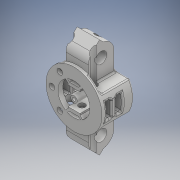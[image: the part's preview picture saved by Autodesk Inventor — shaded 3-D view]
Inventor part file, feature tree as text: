
AUTODESK INVENTOR PART (.ipt)
format: ipt  version: 2018 (Build 220112000, 112)  size: 1,301,504 bytes
history: native  units: mm
features: extrude x27, sketch x27, fillet x7, other x1
ambient origin geometry x8: Origin, YZ Plane, XZ Plane, XY Plane, X Axis, Y Axis, Z Axis, Center Point
bodies: Body1 (feature_tree)
feature tree (62):
  other  "Sólido1"
  extrude  "Extrusión1"  Depth=15.0mm
  extrude  "Extrusión2"  Depth=20.0mm TaperAngle=0.0deg
  extrude  "Extrusión3"  Depth=30.0mm
  extrude  "Extrusión4"  Depth=8.0mm
  extrude  "Extrusión5"  Depth=16.0mm
  extrude  "Extrusión6"  Depth=30.0mm TaperAngle=0.0deg
  extrude  "Extrusión7"  Depth=30.0mm TaperAngle=0.0deg
  extrude  "Extrusión8"  Depth=25.0mm TaperAngle=0.0deg
  extrude  "Extrusión9"  Depth=16.0mm
  extrude  "Extrusión10"  Depth=7.0mm
  extrude  "Extrusión11"  Depth=24.0mm
  extrude  "Extrusión12"  Depth=20.0mm TaperAngle=0.0deg
  extrude  "Extrusión13"  Depth=3.0mm
  extrude  "Extrusión14"  Depth=7.5mm
  extrude  "Extrusión15"  Depth=2.0mm
  fillet  "Empalme1"  Radius=4.0mm
  fillet  "Empalme2"  Radius=4.0mm
  fillet  "Empalme3"  Radius=80.0mm
  fillet  "Empalme4"  Radius=2.0mm
  fillet  "Empalme5"  Radius=20.0mm
  extrude  "Extrusión16"  Depth=2.0mm TaperAngle=0.0deg
  extrude  "Extrusión17"  Depth=5.0mm
  extrude  "Extrusión18"  Depth=3.0mm
  extrude  "Extrusión19"  Depth=40.0mm TaperAngle=0.0deg
  extrude  "Extrusión20"  Depth=1.5mm
  extrude  "Extrusión21"  Depth=10.0mm
  extrude  "Extrusión22"  Depth=10.0mm TaperAngle=0.0deg
  extrude  "Extrusión23"  Depth=1.0mm
  extrude  "Extrusión24"  Depth=1.0mm
  fillet  "Empalme6"  Radius=1.0mm
  extrude  "Extrusión25"  TaperAngle=135.0deg  [1 undecoded]
  fillet  "Empalme7"  Radius=14.0mm
  extrude  "Extrusión26"  TaperAngle=135.0deg  [1 undecoded]
  extrude  "Extrusión27"  Depth=3.0mm TaperAngle=0.0deg
  sketch  "Boceto1"  dims[d0=15.0mm d1=15.0mm]
  sketch  "Boceto2"  dims[d2=35.0mm d3=20.0mm d4=0.0mm]
  sketch  "Boceto3"  dims[d5=15.0mm d6=30.0mm]
  sketch  "Boceto4"  dims[d7=25.0mm d8=0.0mm d9=8.0mm]
  sketch  "Boceto5"  dims[d10=4.0mm d11=16.0mm]
  sketch  "Boceto6"  dims[d12=7.0mm d13=30.0mm d14=0.0mm]
  sketch  "Boceto7"  dims[d15=7.0mm d16=30.0mm d17=0.0mm]
  sketch  "Boceto8"  dims[d18=15.0mm d19=25.0mm d20=0.0mm]
  sketch  "Boceto9"  dims[d21=12.0mm d22=16.0mm]
  sketch  "Boceto10"  dims[d23=30.0mm d24=0.0mm d25=7.0mm]
  sketch  "Boceto11"  dims[d26=30.0mm d27=0.0mm d28=24.0mm]
  sketch  "Boceto12"  dims[d31=24.0mm d32=20.0mm d33=0.0mm]
  sketch  "Boceto13"  dims[d34=3.0mm d35=3.0mm]
  sketch  "Boceto14"  dims[d36=7.5mm d37=7.5mm]
  sketch  "Boceto15"  dims[d38=180.0deg d39=4.0mm d40=4.0mm d41=4.0mm d42=80.0mm d43=0.0mm d44=2.0mm d45=0.0mm d46=20.0mm]
  sketch  "Boceto16"  dims[d47=18.0mm d48=0.0mm d49=2.0mm d50=0.0mm]
  sketch  "Boceto17"  dims[d51=8.0mm d52=5.0mm]
  sketch  "Boceto18"  dims[d53=5.0mm d54=3.0mm]
  sketch  "Boceto19"  dims[d55=5.0mm d56=40.0mm d57=0.0mm]
  sketch  "Boceto20"  dims[d58=1.5mm d59=1.5mm]
  sketch  "Boceto21"  dims[d60=10.0mm d61=0.0mm d62=1.5mm]
  sketch  "Boceto22"  dims[d63=1.5mm d64=10.0mm d65=0.0mm]
  sketch  "Boceto23"  dims[d66=1.0mm d67=1.0mm]
  sketch  "Boceto24"  dims[d68=1.0mm d69=1.0mm d70=1.0mm]
  sketch  "Boceto25"  dims[d71=17.0mm d72=135.0deg d73=14.0mm]
  sketch  "Boceto26"  dims[d74=8.0mm d75=135.0deg]
  sketch  "Boceto27"  dims[d76=2.0mm d77=14.0mm d78=0.0mm d79=40.0mm d80=20.0mm d81=0.0mm d82=0.0mm d86=1.0mm d87=1.0mm d88=1.0mm d89=2.0mm d90=18.0mm d91=0.0mm d92=5.0mm d93=18.0mm d94=0.0mm d95=7.5mm d96=7.0mm d97=0.0mm d98=10.0mm d99=4.0mm d100=2.0mm d101=0.0mm d102=5.0mm d103=4.0mm d104=2.0mm d105=0.0mm d106=15.0mm d107=15.0mm d108=5.0mm d109=0.0mm d110=4.0mm d111=11.0mm d112=0.0mm d113=1.0mm d114=135.0deg d115=135.0deg d116=18.0mm d117=0.0mm d118=1.0mm d130=15.0mm d131=1.0mm d134=7.0mm d136=6.0mm d137=7.0mm d138=5.0mm d139=14.0mm d140=2.0mm d141=14.0mm d142=90.0deg d143=19.0mm d144=5.0mm d145=180.0deg d146=14.0mm d147=2.0mm d150=3.0mm d155=13.25mm d156=180.0deg d161=0.5mm d174=3.5mm d176=13.75mm d177=22.68928mm d178=3.5mm d179=13.75mm d180=22.68928mm d181=3.5mm d184=3.0mm d185=0.0mm d186=2.0mm d187=3.0mm d188=0.0mm]
note: 2 required parameter values undecoded (feature->parameter linkage not recoverable at this tier; creation-order binding heuristic only, values carry confidence <= 0.55)
